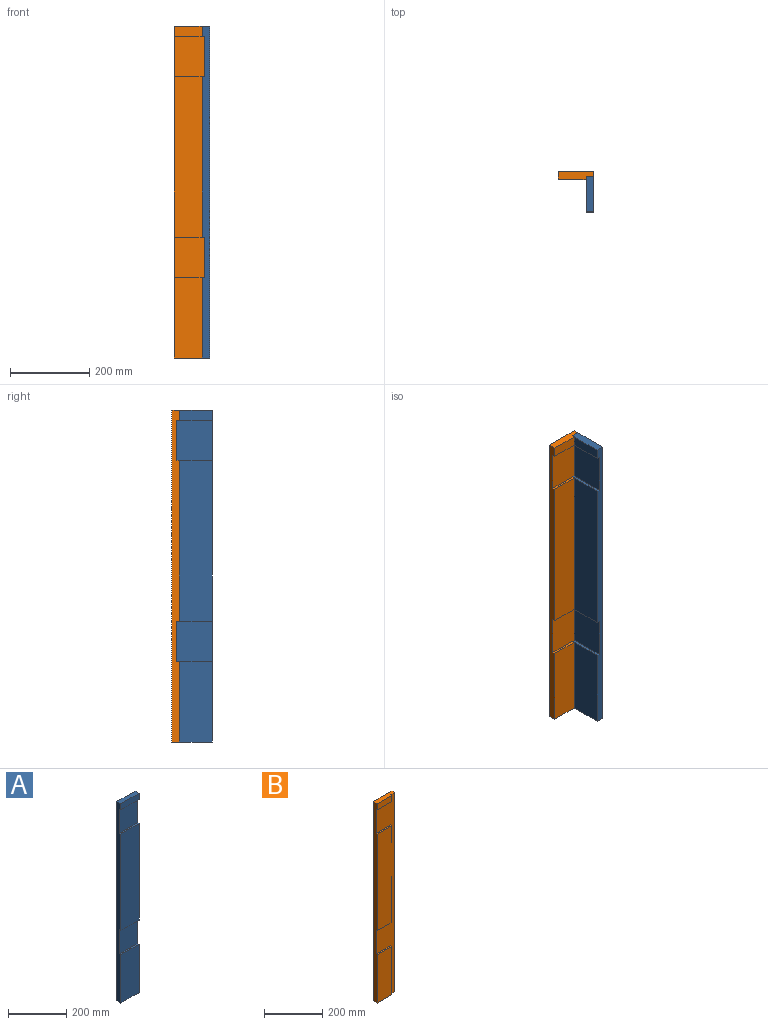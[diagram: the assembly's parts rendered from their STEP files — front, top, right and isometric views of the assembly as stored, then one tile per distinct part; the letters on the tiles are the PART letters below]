
ASSEMBLY  parts=2 mates=1
PART A: 14 faces, bbox 88.9x19.1x838.2 mm
  f0: plane 406.4x88.9mm, normal (0,-1,0), area 36129mm2, adj f2,f3,f8,f12
  f1: plane 203.2x88.9mm, normal (0,-1,0), area 18064.5mm2, adj f2,f3,f6,f9
  f2: plane 838.2x19.05mm, normal (-1,0,0), area 14677.4mm2, adj f0,f1,f4,f5,f6,f7,f8,f9
  f3: plane 838.2x19.05mm, normal (1,0,0), area 14677.4mm2, adj f0,f1,f4,f5,f6,f7,f8,f9
  f4: plane 838.2x88.9mm, normal (0,1,0), area 74516mm2, adj f2,f3,f6,f7
  f5: plane 88.9x25.4mm, normal (0,-1,0), area 2258.1mm2, adj f2,f3,f7,f11
  f6: plane 88.9x19.05mm, normal (0,0,-1), area 1693.5mm2, adj f1,f2,f3,f4
  f7: plane 88.9x19.05mm, normal (0,0,1), area 1693.5mm2, adj f2,f3,f4,f5
  f8: plane 88.9x6.35mm, normal (0,0,-1), area 564.5mm2, adj f0,f2,f3,f10
  f9: plane 88.9x6.35mm, normal (0,0,1), area 564.5mm2, adj f1,f2,f3,f10
  f10: plane 101.6x88.9mm, normal (0,-1,0), area 9032.2mm2, adj f2,f3,f8,f9
  f11: plane 88.9x6.35mm, normal (0,0,-1), area 564.5mm2, adj f2,f3,f5,f13
  f12: plane 88.9x6.35mm, normal (0,0,1), area 564.5mm2, adj f0,f2,f3,f13
  f13: plane 101.6x88.9mm, normal (0,-1,0), area 9032.2mm2, adj f2,f3,f11,f12
PART B: 16 faces, bbox 88.9x19.1x838.2 mm
  f0: plane 406.4x69.85mm, normal (0,-1,0), area 28387mm2, adj f2,f6,f12,f15
  f1: plane 203.2x69.85mm, normal (0,-1,0), area 14193.5mm2, adj f3,f6,f8,f13
  f2: plane 406.4x6.35mm, normal (1,0,0), area 2580.6mm2, adj f0,f10,f12,f15
  f3: plane 203.2x6.35mm, normal (1,0,0), area 1290.3mm2, adj f1,f8,f10,f13
  f4: plane 838.2x12.7mm, normal (1,0,0), area 10645.1mm2, adj f5,f8,f9,f10
  f5: plane 838.2x88.9mm, normal (0,1,0), area 74516mm2, adj f4,f6,f8,f9
  f6: plane 838.2x19.05mm, normal (-1,0,0), area 14677.4mm2, adj f0,f1,f5,f7,f8,f9,f10,f12
  f7: plane 69.85x25.4mm, normal (0,-1,0), area 1774.2mm2, adj f6,f9,f11,f14
  f8: plane 88.9x19.05mm, normal (0,0,-1), area 1572.6mm2, adj f1,f3,f4,f5,f6,f10
  f9: plane 88.9x19.05mm, normal (0,0,1), area 1572.6mm2, adj f4,f5,f6,f7,f10,f11
  f10: plane 838.2x88.9mm, normal (0,-1,0), area 30161.2mm2, adj f2,f3,f4,f6,f8,f9,f11,f12
  f11: plane 25.4x6.35mm, normal (1,0,0), area 161.3mm2, adj f7,f9,f10,f14
  f12: plane 69.85x6.35mm, normal (0,0,-1), area 443.5mm2, adj f0,f2,f6,f10
  f13: plane 69.85x6.35mm, normal (0,0,1), area 443.5mm2, adj f1,f3,f6,f10
  f14: plane 69.85x6.35mm, normal (0,0,-1), area 443.5mm2, adj f6,f7,f10,f11
  f15: plane 69.85x6.35mm, normal (0,0,1), area 443.5mm2, adj f0,f2,f6,f10
PLACE A rot(axis=(0,0,-1),90deg) t=(179.05,-152.51,136.96)mm fixed
PLACE B t=(144.13,-104.88,136.96)mm
MATE fastened B.f10 <-> A.f2  axis (0,-1,0) through (188.58,-108.06,136.96)mm
